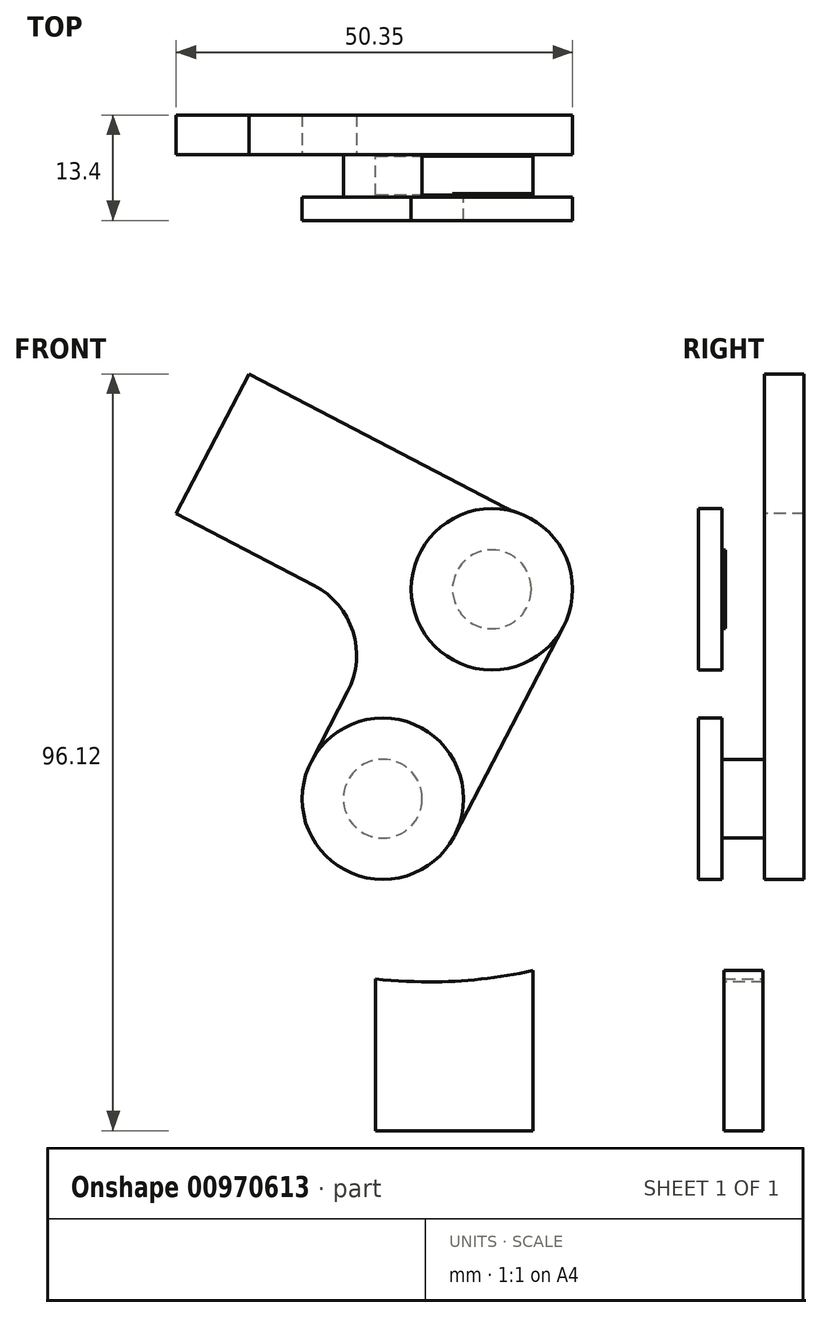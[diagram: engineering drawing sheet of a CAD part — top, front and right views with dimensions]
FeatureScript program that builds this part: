
annotation { "Feature Type Name" : "Feature", "Feature Type Description" : "" }
export const myFeature = defineFeature(function(context is Context, id is Id, definition is map)
    precondition{}
    {
        {
            assignVariable(context, id + "F0", {"name" : "Tbrace", "anyValue" : 5});
        }
        {
            assignVariable(context, id + "F1", {"name" : "Zclearance", "anyValue" : 0.2});
        }
        {
            assignVariable(context, id + "F2", {"name" : "Hpin", "anyValue" : getVariable(context, 'Tbrace') + 2 * getVariable(context, 'Zclearance')});
        }
        {
            assignVariable(context, id + "F3", {"name" : "Tcap", "anyValue" : 3});
        }
        {
            var Q0;
            Q0=qCreatedBy(makeId("Front.planeOp"),FACE);
            var sketch = newSketch(context, id + "F4", { "sketchPlane" : qUnion([Q0])});
            skCircle(sketch, "E0", {"center": v(0, 0) * mm, "radius": 5 * mm});
            skCircle(sketch, "E1", {"center": v(-30, 0) * mm, "radius": 5 * mm});
            skLineSegment(sketch, "E2", {"start": v(0, 0) * mm, "end": v(-30, 0) * mm, "construction": true});
            skSolve(sketch);
        }
        {
            var Q0;
            Q0=qCreatedBy(makeId("Front.planeOp"),FACE);
            var sketch = newSketch(context, id + "F5", { "sketchPlane" : qUnion([Q0])});
            skArc(sketch, "E3", {"start": v(0, 0) * mm, "mid": v(4.76, 8.78) * mm, "end": v(7.87, 18.27) * mm, "construction": true});
            skLineSegment(sketch, "E4", {"start": v(-46.2, 30.74) * mm, "end": v(0, 0) * mm, "construction": true});
            skLineSegment(sketch, "E5", {"start": v(-46.2, 30.74) * mm, "end": v(7.87, 18.27) * mm, "construction": true});
            skArc(sketch, "E6.0.startCap", {"start": v(4.37, -2.9) * mm, "mid": v(-2.9, -4.37) * mm, "end": v(-4.37, 2.9) * mm});
            skArc(sketch, "E6.0.endCap", {"start": v(2.76, 19.45) * mm, "mid": v(9.05, 23.38) * mm, "end": v(12.99, 17.09) * mm});
            skArc(sketch, "E6.0.left", {"start": v(-4.37, 2.9) * mm, "mid": v(-0.06, 10.86) * mm, "end": v(2.76, 19.45) * mm});
            skArc(sketch, "E6.0.right", {"start": v(4.37, -2.9) * mm, "mid": v(9.58, 6.7) * mm, "end": v(12.99, 17.09) * mm});
            skPoint(sketch, "E7", {"position": v(25.08, -6.3) * mm});
            skLineSegment(sketch, "E8", {"start": v(7.87, 18.27) * mm, "end": v(25.08, -6.3) * mm, "construction": true});
            skLineSegment(sketch, "E9.1.0", {"start": v(-46.2, 30.74) * mm, "end": v(1.08, 1.68) * mm, "construction": true});
            skLineSegment(sketch, "E9.2.0", {"start": v(-46.2, 30.74) * mm, "end": v(2.1, 3.4) * mm, "construction": true});
            skLineSegment(sketch, "E9.3.0", {"start": v(-46.2, 30.74) * mm, "end": v(3.05, 5.17) * mm, "construction": true});
            skLineSegment(sketch, "E9.4.0", {"start": v(-46.2, 30.74) * mm, "end": v(3.94, 6.96) * mm, "construction": true});
            skLineSegment(sketch, "E9.5.0", {"start": v(-46.2, 30.74) * mm, "end": v(4.76, 8.78) * mm, "construction": true});
            skLineSegment(sketch, "E9.6.0", {"start": v(-46.2, 30.74) * mm, "end": v(5.52, 10.63) * mm, "construction": true});
            skLineSegment(sketch, "E9.7.0", {"start": v(-46.2, 30.74) * mm, "end": v(6.21, 12.5) * mm, "construction": true});
            skLineSegment(sketch, "E9.8.0", {"start": v(-46.2, 30.74) * mm, "end": v(6.84, 14.4) * mm, "construction": true});
            skLineSegment(sketch, "E9.9.0", {"start": v(-46.2, 30.74) * mm, "end": v(7.39, 16.33) * mm, "construction": true});
            skLineSegment(sketch, "E10", {"start": v(7.39, 16.33) * mm, "end": v(18.87, -11.39) * mm, "construction": true});
            skLineSegment(sketch, "E11", {"start": v(6.84, 14.4) * mm, "end": v(12.04, -15.14) * mm, "construction": true});
            skLineSegment(sketch, "E12", {"start": v(6.21, 12.5) * mm, "end": v(4.9, -17.47) * mm, "construction": true});
            skLineSegment(sketch, "E13", {"start": v(5.52, 10.63) * mm, "end": v(-2.24, -18.35) * mm, "construction": true});
            skLineSegment(sketch, "E14", {"start": v(4.76, 8.78) * mm, "end": v(-9.1, -17.83) * mm, "construction": true});
            skLineSegment(sketch, "E15", {"start": v(3.94, 6.96) * mm, "end": v(-15.35, -16.02) * mm, "construction": true});
            skLineSegment(sketch, "E16", {"start": v(3.05, 5.17) * mm, "end": v(-20.75, -13.1) * mm, "construction": true});
            skLineSegment(sketch, "E17", {"start": v(2.1, 3.4) * mm, "end": v(-25.1, -9.27) * mm, "construction": true});
            skLineSegment(sketch, "E18", {"start": v(1.08, 1.68) * mm, "end": v(-28.21, -4.8) * mm, "construction": true});
            skLineSegment(sketch, "E19", {"start": v(0, 0) * mm, "end": v(-30, 0) * mm, "construction": true});
            skFitSpline(sketch, "E20", {"points": [v(-30, 0) * mm, v(-28.21, -4.8) * mm, v(-25.1, -9.27) * mm, v(-20.75, -13.1) * mm, v(-15.35, -16.02) * mm, v(-9.1, -17.83) * mm, v(-2.24, -18.35) * mm, v(4.9, -17.47) * mm, v(12.04, -15.14) * mm, v(18.87, -11.39) * mm, v(25.08, -6.3) * mm], "startDerivative": vector(0, -79.8) * mm, "endDerivative": vector(58.42, 58.42) * mm, "construction": true});
            skLineSegment(sketch, "E21.0.startCap", {"start": v(-35.25, 0) * mm, "end": v(-35.25, 0) * mm});
            skLineSegment(sketch, "E21.0.endCap", {"start": v(28.8, -10.02) * mm, "end": v(28.8, -10.02) * mm});
            skFitSpline(sketch, "E21.0.left", {"points": [v(-48, 0) * mm, v(-48, -0.78) * mm, v(-47.9, -2.28) * mm, v(-47.5, -4.33) * mm, v(-46.97, -6.18) * mm, v(-46.46, -7.56) * mm, v(-46.03, -8.58) * mm, v(-45.71, -9.3) * mm, v(-45.45, -9.88) * mm, v(-45.24, -10.32) * mm, v(-45.04, -10.74) * mm, v(-44.78, -11.28) * mm, v(-44.34, -12.15) * mm, v(-43.77, -13.24) * mm, v(-43.02, -14.57) * mm, v(-42.22, -15.9) * mm, v(-41.49, -17) * mm, v(-40.86, -17.88) * mm, v(-40.21, -18.76) * mm, v(-39.37, -19.83) * mm, v(-38.3, -21.06) * mm, v(-37.19, -22.25) * mm, v(-35.65, -23.76) * mm, v(-33.63, -25.52) * mm, v(-30.22, -28.1) * mm, v(-26.52, -30.33) * mm, v(-22.58, -32.16) * mm, v(-18.53, -33.72) * mm, v(-13.25, -35.16) * mm, v(-6.74, -36.05) * mm, v(-1.22, -36.1) * mm, v(3.19, -35.74) * mm, v(7.6, -35.1) * mm, v(11.94, -34.06) * mm, v(16.16, -32.67) * mm, v(19.25, -31.44) * mm, v(22.28, -30.04) * mm, v(24.76, -28.7) * mm, v(26.73, -27.55) * mm, v(28.69, -26.32) * mm, v(31.12, -24.67) * mm, v(33.92, -22.52) * mm, v(35.65, -20.98) * mm, v(36.47, -20.15) * mm]});
            skFitSpline(sketch, "E21.0.right", {"points": [v(-48, 0) * mm, v(-48, -0.78) * mm, v(-47.9, -2.28) * mm, v(-47.5, -4.33) * mm, v(-46.97, -6.18) * mm, v(-46.46, -7.56) * mm, v(-46.03, -8.58) * mm, v(-45.71, -9.3) * mm, v(-45.45, -9.88) * mm, v(-45.24, -10.32) * mm, v(-45.04, -10.74) * mm, v(-44.78, -11.28) * mm, v(-44.34, -12.15) * mm, v(-43.77, -13.24) * mm, v(-43.02, -14.57) * mm, v(-42.22, -15.9) * mm, v(-41.49, -17) * mm, v(-40.86, -17.88) * mm, v(-40.21, -18.76) * mm, v(-39.37, -19.83) * mm, v(-38.3, -21.06) * mm, v(-37.19, -22.25) * mm, v(-35.65, -23.76) * mm, v(-33.63, -25.52) * mm, v(-30.22, -28.1) * mm, v(-26.52, -30.33) * mm, v(-22.58, -32.16) * mm, v(-18.53, -33.72) * mm, v(-13.25, -35.16) * mm, v(-6.74, -36.05) * mm, v(-1.22, -36.1) * mm, v(3.19, -35.74) * mm, v(7.6, -35.1) * mm, v(11.94, -34.06) * mm, v(16.16, -32.67) * mm, v(19.25, -31.44) * mm, v(22.28, -30.04) * mm, v(24.76, -28.7) * mm, v(26.73, -27.55) * mm, v(28.69, -26.32) * mm, v(31.12, -24.67) * mm, v(33.92, -22.52) * mm, v(35.65, -20.98) * mm, v(36.47, -20.15) * mm]});
            skFitSpline(sketch, "E22.0", {"points": [v(-32, 0) * mm, v(-32, -0.05) * mm, v(-32, -0.17) * mm, v(-31.96, -0.4) * mm, v(-31.92, -0.6) * mm, v(-31.85, -0.86) * mm, v(-31.76, -1.16) * mm, v(-31.64, -1.5) * mm, v(-31.5, -1.86) * mm, v(-31.33, -2.27) * mm, v(-31.14, -2.7) * mm, v(-30.92, -3.18) * mm, v(-30.68, -3.69) * mm, v(-30.43, -4.19) * mm, v(-30.1, -4.83) * mm, v(-29.7, -5.62) * mm, v(-29.2, -6.5) * mm, v(-28.69, -7.35) * mm, v(-28.16, -8.14) * mm, v(-27.63, -8.89) * mm, v(-27.05, -9.61) * mm, v(-26.42, -10.34) * mm, v(-25.75, -11.05) * mm, v(-25.04, -11.75) * mm, v(-24.3, -12.43) * mm, v(-23.51, -13.1) * mm, v(-22.7, -13.73) * mm, v(-21.58, -14.54) * mm, v(-20.41, -15.3) * mm, v(-19.2, -16) * mm, v(-17.95, -16.67) * mm, v(-16.33, -17.42) * mm, v(-13.64, -18.46) * mm, v(-10.78, -19.24) * mm, v(-7.83, -19.74) * mm, v(-4.8, -20.06) * mm, v(-1.72, -20.09) * mm, v(1.38, -19.83) * mm, v(3.72, -19.5) * mm, v(6.07, -19) * mm, v(8.4, -18.38) * mm, v(10.7, -17.62) * mm, v(12.92, -16.74) * mm, v(14.75, -15.9) * mm, v(16.2, -15.13) * mm, v(17.31, -14.52) * mm, v(18.43, -13.87) * mm, v(19.56, -13.16) * mm, v(20.67, -12.43) * mm, v(21.75, -11.67) * mm, v(22.6, -11.04) * mm, v(23.23, -10.55) * mm, v(23.68, -10.18) * mm, v(24.1, -9.82) * mm, v(24.62, -9.36) * mm, v(24.96, -9.04) * mm, v(25.16, -8.84) * mm]});
            skArc(sketch, "E23", {"start": v(-35.25, 0) * mm, "mid": v(-30, 5.25) * mm, "end": v(-24.75, 0) * mm});
            skArc(sketch, "E24", {"start": v(28.8, -10.02) * mm, "mid": v(28.8, -2.6) * mm, "end": v(21.37, -2.6) * mm});
            skLineSegment(sketch, "E25", {"start": v(25.08, -6.3) * mm, "end": v(22.93, -8.45) * mm, "construction": true});
            skSolve(sketch);
        }
        {
            var Q0;
            Q0=qCreatedBy(makeId("Front.planeOp"),FACE);
            var sketch = newSketch(context, id + "F6", { "sketchPlane" : qUnion([Q0])});
            skArc(sketch, "E26", {"start": v(-30, 10.25) * mm, "mid": v(-40.25, 0) * mm, "end": v(-30, -10.25) * mm});
            skArc(sketch, "E27", {"start": v(0, -10.25) * mm, "mid": v(7.8, -6.66) * mm, "end": v(10.12, 1.6) * mm});
            skLineSegment(sketch, "E28", {"start": v(-30, -10.25) * mm, "end": v(0, -10.25) * mm});
            skLineSegment(sketch, "E29", {"start": v(-30, 10.25) * mm, "end": v(-20, 10.25) * mm});
            skLineSegment(sketch, "E30", {"start": v(-10, 20.25) * mm, "end": v(-10, 40) * mm});
            skLineSegment(sketch, "E31", {"start": v(10, 3.17) * mm, "end": v(10, 40) * mm});
            skLineSegment(sketch, "E32", {"start": v(10, 40) * mm, "end": v(-10, 40) * mm});
            skPoint(sketch, "E33", {"position": v(0, 40) * mm});
            skPoint(sketch, "E34.visualSharp", {"position": v(10, 2.25) * mm});
            skArc(sketch, "E34.filletArc", {"start": v(10, 3.17) * mm, "mid": v(10.03, 2.39) * mm, "end": v(10.12, 1.6) * mm});
            skPoint(sketch, "E35.visualSharp", {"position": v(-10, 10.25) * mm});
            skArc(sketch, "E35.filletArc", {"start": v(-20, 10.25) * mm, "mid": v(-12.93, 13.18) * mm, "end": v(-10, 20.25) * mm});
            skSolve(sketch);
        }
        {
            var Q0;
            Q0=qCreatedBy(makeId("Front.planeOp"),FACE);
            var sketch = newSketch(context, id + "F7", { "sketchPlane" : qUnion([Q0])});
            skArc(sketch, "E36", {"start": v(-34.45, 9.23) * mm, "mid": v(-38.68, 5.45) * mm, "end": v(-40.25, 0) * mm});
            skArc(sketch, "E37", {"start": v(32.33, -13.55) * mm, "mid": v(35.3, -7.2) * mm, "end": v(33.48, -0.43) * mm});
            skArc(sketch, "E38", {"start": v(16.27, 24.15) * mm, "mid": v(10.46, 28.19) * mm, "end": v(3.42, 27.5) * mm});
            skFitSpline(sketch, "E39.0", {"points": [v(-53, 0) * mm, v(-53, -1) * mm, v(-52.86, -2.92) * mm, v(-52.38, -5.5) * mm, v(-51.72, -7.76) * mm, v(-51.12, -9.39) * mm, v(-50.63, -10.56) * mm, v(-50.27, -11.37) * mm, v(-49.98, -12) * mm, v(-49.76, -12.47) * mm, v(-49.54, -12.92) * mm, v(-49.26, -13.5) * mm, v(-48.79, -14.44) * mm, v(-48.16, -15.63) * mm, v(-47.34, -17.08) * mm, v(-46.45, -18.57) * mm, v(-45.62, -19.81) * mm, v(-44.92, -20.81) * mm, v(-44.18, -21.81) * mm, v(-43.22, -23.02) * mm, v(-42.01, -24.42) * mm, v(-40.76, -25.74) * mm, v(-39.47, -27.01) * mm, v(-38.14, -28.22) * mm, v(-36.78, -29.38) * mm, v(-35.37, -30.48) * mm, v(-33.45, -31.88) * mm, v(-30.95, -33.5) * mm, v(-27.8, -35.25) * mm, v(-24.54, -36.77) * mm, v(-21.18, -38.06) * mm, v(-17.74, -39.12) * mm, v(-13.06, -40.23) * mm, v(-8.29, -40.89) * mm, v(-3.48, -41.08) * mm, v(0.14, -41) * mm, v(3.75, -40.71) * mm, v(7.36, -40.19) * mm, v(10.93, -39.45) * mm, v(14.43, -38.5) * mm, v(17.87, -37.37) * mm, v(21.23, -36.04) * mm, v(24.52, -34.5) * mm, v(27.74, -32.78) * mm, v(30.9, -30.87) * mm, v(34.04, -28.73) * mm, v(37.1, -26.39) * mm, v(39.05, -24.65) * mm, v(40, -23.69) * mm]});
            skLineSegment(sketch, "E40", {"start": v(-34.45, 9.23) * mm, "end": v(3.42, 27.5) * mm});
            skLineSegment(sketch, "E41", {"start": v(16.27, 24.15) * mm, "end": v(33.48, -0.43) * mm});
            skLineSegment(sketch, "E42", {"start": v(-10, -35.89) * mm, "end": v(-10, -60) * mm});
            skLineSegment(sketch, "E43", {"start": v(10, -33.76) * mm, "end": v(10, -60) * mm});
            skLineSegment(sketch, "E44", {"start": v(10, -60) * mm, "end": v(-10, -60) * mm});
            skPoint(sketch, "E45", {"position": v(0, -60) * mm});
            skFitSpline(sketch, "E46.trimOffspring", {"points": [v(-53, 0) * mm, v(-53, -1) * mm, v(-52.86, -2.92) * mm, v(-52.38, -5.5) * mm, v(-51.72, -7.76) * mm, v(-51.12, -9.39) * mm, v(-50.63, -10.56) * mm, v(-50.27, -11.37) * mm, v(-49.98, -12) * mm, v(-49.76, -12.47) * mm, v(-49.54, -12.92) * mm, v(-49.26, -13.5) * mm, v(-48.79, -14.44) * mm, v(-48.16, -15.63) * mm, v(-47.34, -17.08) * mm, v(-46.45, -18.57) * mm, v(-45.62, -19.81) * mm, v(-44.92, -20.81) * mm, v(-44.18, -21.81) * mm, v(-43.22, -23.02) * mm, v(-42.01, -24.42) * mm, v(-40.76, -25.74) * mm, v(-39.47, -27.01) * mm, v(-38.14, -28.22) * mm, v(-36.78, -29.38) * mm, v(-35.37, -30.48) * mm, v(-33.45, -31.88) * mm, v(-30.95, -33.5) * mm, v(-27.8, -35.25) * mm, v(-24.54, -36.77) * mm, v(-21.18, -38.06) * mm, v(-17.74, -39.12) * mm, v(-13.06, -40.23) * mm, v(-8.29, -40.89) * mm, v(-3.48, -41.08) * mm, v(0.14, -41) * mm, v(3.75, -40.71) * mm, v(7.36, -40.19) * mm, v(10.93, -39.45) * mm, v(14.43, -38.5) * mm, v(17.87, -37.37) * mm, v(21.23, -36.04) * mm, v(24.52, -34.5) * mm, v(27.74, -32.78) * mm, v(30.9, -30.87) * mm, v(34.04, -28.73) * mm, v(37.1, -26.39) * mm, v(39.05, -24.65) * mm, v(40, -23.69) * mm]});
            skPoint(sketch, "E47.visualSharp", {"position": v(-10, -28.07) * mm});
            skArc(sketch, "E47.filletArc", {"start": v(-10, -35.89) * mm, "mid": v(-11.88, -30.05) * mm, "end": v(-16.81, -26.41) * mm});
            skPoint(sketch, "E48.visualSharp", {"position": v(10, -26.74) * mm});
            skArc(sketch, "E48.filletArc", {"start": v(16.02, -24.59) * mm, "mid": v(11.64, -28.28) * mm, "end": v(10, -33.76) * mm});
            skSolve(sketch);
        }
        {
            var Q0;
            Q0=qSketchRegion(id+"F6",true);
            extrude(context, id + "F8", {"entities" : qUnion([Q0]), "oppositeDirection" : true, "depth" : (getVariable(context, 'Tbrace')) * mm, "offsetDistance" : 25 * mm});
        }
        {
            var Q0;
            Q0=qSketchRegion(id+"F4",true);
            extrude(context, id + "F9", {"entities" : qUnion([Q0]), "operationType" : NewBodyOperationType.ADD, "depth" : (getVariable(context, 'Hpin')) * mm, "offsetDistance" : 25 * mm});
        }
        {
            var Q0;
            Q0=qSketchRegion(id+"F7",true);
            extrude(context, id + "F10", {"entities" : qUnion([Q0]), "depth" : (getVariable(context, 'Tbrace')) * mm, "offsetDistance" : 25 * mm});
        }
        {
            var Q0;
            Q0=qSketchRegion(id+"F5",true);
            var Q1;
            Q1=makeQuery(id+"F10.opExtrude","CAP_FACE",FACE,{"disambiguationData":[OSD([sQuery(id+"F7.wireOp",EDGE,"E36"),sQuery(id+"F7.wireOp",EDGE,"E37"),sQuery(id+"F7.wireOp",EDGE,"E38"),sQuery(id+"F7.wireOp",EDGE,"E39.0"),sQuery(id+"F7.wireOp",EDGE,"E40"),sQuery(id+"F7.wireOp",EDGE,"E41"),sQuery(id+"F7.wireOp",EDGE,"E42"),sQuery(id+"F7.wireOp",EDGE,"E43"),sQuery(id+"F7.wireOp",EDGE,"E44"),sQuery(id+"F7.wireOp",EDGE,"E46.trimOffspring"),sQuery(id+"F7.wireOp",EDGE,"E47.filletArc"),sQuery(id+"F7.wireOp",EDGE,"E48.filletArc")])],"isStart":false});
            extrude(context, id + "F11", {"entities" : qUnion([Q0]), "operationType" : NewBodyOperationType.REMOVE, "endBound" : BoundingType.UP_TO_SURFACE, "depth" : 25 * mm, "endBoundEntityFace" : qUnion([Q1]), "offsetDistance" : 25 * mm});
        }
        {
            var Q0;
            Q0=makeQuery(id+"F10.opExtrude","SWEPT_BODY",BODY,{"disambiguationData":[OSD([sQuery(id+"F7.wireOp",EDGE,"E36"),sQuery(id+"F7.wireOp",EDGE,"E37"),sQuery(id+"F7.wireOp",EDGE,"E38"),sQuery(id+"F7.wireOp",EDGE,"E39.0"),sQuery(id+"F7.wireOp",EDGE,"E40"),sQuery(id+"F7.wireOp",EDGE,"E41"),sQuery(id+"F7.wireOp",EDGE,"E42"),sQuery(id+"F7.wireOp",EDGE,"E43"),sQuery(id+"F7.wireOp",EDGE,"E44"),sQuery(id+"F7.wireOp",EDGE,"E46.trimOffspring"),sQuery(id+"F7.wireOp",EDGE,"E47.filletArc"),sQuery(id+"F7.wireOp",EDGE,"E48.filletArc")])]});
            transform(context, id + "F12", {"entities" : qUnion([Q0]), "transformType" : TransformType.TRANSLATION_3D, "dx" : 0 * mm, "dy" : (-getVariable(context, 'Zclearance')) * mm, "dz" : 0 * mm, "makeCopy" : false});
        }
        {
            var Q0;
            Q0=makeQuery(id+"F9.opExtrude","CAP_FACE",FACE,{"disambiguationData":[OSD([sQuery(id+"F4.wireOp",EDGE,"E0")])],"isStart":false});
            var sketch = newSketch(context, id + "F13", { "sketchPlane" : qUnion([Q0])});
            skCircle(sketch, "E49", {"center": v(0, 0) * mm, "radius": 10.25 * mm});
            skCircle(sketch, "E50", {"center": v(-30, 0) * mm, "radius": 10.25 * mm});
            skSolve(sketch);
        }
        {
            var Q0;
            Q0=qSketchRegion(id+"F13",true);
            extrude(context, id + "F14", {"entities" : qUnion([Q0]), "operationType" : NewBodyOperationType.ADD, "depth" : (getVariable(context, 'Tcap')) * mm, "offsetDistance" : 25 * mm});
        }
        {
            var Q0;
            Q0=qCreatedBy(makeId("Front.planeOp"),FACE);
            var sketch = newSketch(context, id + "F15", { "sketchPlane" : qUnion([Q0])});
            skPoint(sketch, "E51", {"position": v(4.76, 8.78) * mm});
            skPoint(sketch, "E52", {"position": v(-9.1, -17.83) * mm});
            skLineSegment(sketch, "E53", {"start": v(4.76, 8.78) * mm, "end": v(-9.1, -17.83) * mm, "construction": true});
            skSolve(sketch);
        }
        {
            var Q0;
            Q0=qCreatedBy(makeId("Top.planeOp"),FACE);
            var sketch = newSketch(context, id + "F16", { "sketchPlane" : qUnion([Q0])});
            skLineSegment(sketch, "E54", {"start": v(0, 9.69) * mm, "end": v(0, -16.2) * mm, "construction": true});
            skSolve(sketch);
        }
        {
            var Q0;
            Q0=makeQuery(id+"F8.opExtrude","SWEPT_BODY",BODY,{"disambiguationData":[OSD([sQuery(id+"F6.wireOp",EDGE,"E26"),sQuery(id+"F6.wireOp",EDGE,"E27"),sQuery(id+"F6.wireOp",EDGE,"E28"),sQuery(id+"F6.wireOp",EDGE,"E29"),sQuery(id+"F6.wireOp",EDGE,"E30"),sQuery(id+"F6.wireOp",EDGE,"E31"),sQuery(id+"F6.wireOp",EDGE,"E32"),sQuery(id+"F6.wireOp",EDGE,"E34.filletArc"),sQuery(id+"F6.wireOp",EDGE,"E35.filletArc")])]});
            var Q1;
            Q1=sQuery(id+"F16.wireOp",EDGE,"E54");
            transform(context, id + "F17", {"entities" : qUnion([Q0]), "transformType" : TransformType.ROTATION, "transformAxis" : qUnion([Q1]), "angle" : 62.5 * degree, "makeCopy" : false});
        }
        {
            var Q0;
            Q0=makeQuery(id+"F8.opExtrude","SWEPT_BODY",BODY,{"disambiguationData":[OSD([sQuery(id+"F6.wireOp",EDGE,"E26"),sQuery(id+"F6.wireOp",EDGE,"E27"),sQuery(id+"F6.wireOp",EDGE,"E28"),sQuery(id+"F6.wireOp",EDGE,"E29"),sQuery(id+"F6.wireOp",EDGE,"E30"),sQuery(id+"F6.wireOp",EDGE,"E31"),sQuery(id+"F6.wireOp",EDGE,"E32"),sQuery(id+"F6.wireOp",EDGE,"E34.filletArc"),sQuery(id+"F6.wireOp",EDGE,"E35.filletArc")])]});
            var Q1;
            Q1=sQuery(id+"F5.wireOp",VERTEX,"E3.start");
            var Q2;
            Q2=sQuery(id+"F15.wireOp",VERTEX,"E51");
            transform(context, id + "F18", {"entities" : qUnion([Q0]), "transformType" : TransformType.TRANSLATION_ENTITY, "oppositeDirectionEntity" : false, "transformLine" : qUnion([Q1, Q2]), "makeCopy" : false});
        }
    });
